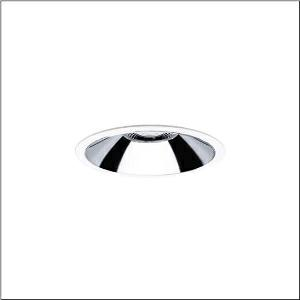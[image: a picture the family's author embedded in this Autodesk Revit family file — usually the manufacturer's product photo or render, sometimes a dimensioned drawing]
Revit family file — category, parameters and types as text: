
# Revit family: lunis_21_xl_51db15df43
name_source: partatom
category: Lighting Fixtures
units: mm (PartAtom-declared; Revit-internal decimal feet)

## family parameters
Cut with Voids When Loaded = No
Host = Face
Light Source = No
Part Type = Normal
Room Calculation Point = No
Round Connector Dimension = Use Diameter
Shared = No

## types (1)
- Lunis 21 XL (1 x LED, 3560 lm, 31 W, 4000K)
    Apparent Load = 31 VA
    CIE Flux Codes = 89 99 100 100 100
    Color Rendering = 80
    Color Temperature = 4000K
    Default Elevation = 1800 mm
    Description = Lunis 21,  XL, downlight, of PC, light emission: direct distribution, LED rated luminous flux: 3.560lm, light colour: 840, control gear: ECG DALI, with terminal, 5-pole, mains connection: 220..240V, AC, housing, round, of diecast aluminium, traffic white (RAL 9016), diameter: 213mm, protection rating (complete): IP20, protection rating (on room side): IP54, insulation class (complete): insulation class II (safety insulation), certification: CE, impact resistance: IK02, packaging unit: 1 piece
    Height = 0 mm  [stored 0 ft]
    Lamp = 1 x LED
    Lamp Light Flux = 3560 lm
    Lamp Power = 31 W
    Lamp count = 1
    Length = 213 mm
    Luminous efficacy = 115 lm/W
    Manufacturer = Siteco
    ModVariant = No
    Model = 51DB15DF43
    Mounting Place = Ceiling
    Mounting Type = Recessed
    Number of Poles = 1
    OnlyDefault = Yes
    Power Factor = 1
    Product Name = Lunis 21 XL
    Product group = downlight
    ProductGroupID = 400
    Protection Class = Protection class II
    Protection Degree = IP 20
    RLX_Detail_Level = 1
    RLX_Emergency_Light_Flux = 0 lm
    RLX_Emergency_Type = 0
    RLX_Emergency_Type_DB = No
    RlxData = <blob elided: 26957 chars, md5=f79939ac>
    Socket = socket
    Standby Power = 0 W
    System Light Flux = 3560 lm
    System Power = 31 W
    Type Comments = Product without accessories
    Type Image = l_1287385.jpg
    URL = http://relux.com
    VarID = ---
    Voltage = 0 V
    Weight = 0.00 kg
    Width = 0 mm  [stored 0 ft]

note: [stored X ft] marks values corroborated as IEEE doubles in the binary element streams (Revit-internal decimal feet)

## geometry (parser evidence)
native form markers: Blend x4, Sweep x11
no freeform markers — native parametric forms only
